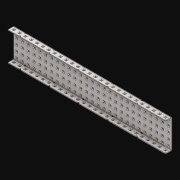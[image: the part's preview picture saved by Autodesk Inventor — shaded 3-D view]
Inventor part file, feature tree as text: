
AUTODESK INVENTOR PART (.ipt)
format: ipt  version: 2021 (Build 250183000, 183)  size: 3,673,600 bytes
history: native  units: in
note: dims shown in document units (in); Inventor stores cm internally (conversion verified against a paired STEP export)
features: extrude x190, other x189, sketch x4, thicken_offset x3, pattern_linear x3, imported_body x1
ambient origin geometry x8: Origin, YZ Plane, XZ Plane, XY Plane, X Axis, Y Axis, Z Axis, Center Point
bodies: Solid1 (feature_tree)
feature tree (390):
  thicken_offset  "Thicken1"
  thicken_offset  "Thicken2"
  thicken_offset  "Thicken3"
  pattern_linear  "Rectangular Pattern1"  Spacing1=0.001in  [1 undecoded]
  pattern_linear  "Rectangular Pattern2"  Spacing1=0.001in  [1 undecoded]
  pattern_linear  "Rectangular Pattern3"  Spacing1=0.182in  [1 undecoded]
  extrude  "Extrusion1"  Depth=0.063in TaperAngle=0.0deg
  sketch  "Sketch1"  dims[d0=0.001in]
  other  "Srf1"
  sketch  "Sketch2"  dims[d1=0.001in]
  other  "Srf2"
  sketch  "Sketch3"  dims[d2=0.001in]
  other  "Srf3"
  other  "Srf4"
  other  "Srf5"
  other  "Srf6"
  other  "Srf7"
  other  "Srf8"
  other  "Srf9"
  other  "Srf10"
  other  "Srf11"
  other  "Srf12"
  other  "Srf13"
  other  "Srf14"
  other  "Srf15"
  other  "Srf16"
  other  "Srf17"
  other  "Srf18"
  other  "Srf19"
  other  "Srf20"
  other  "Srf21"
  other  "Srf22"
  other  "Srf23"
  other  "Srf24"
  other  "Srf25"
  other  "Srf26"
  other  "Srf27"
  other  "Srf28"
  other  "Srf29"
  other  "Srf38"
  other  "Srf39"
  other  "Srf40"
  other  "Srf41"
  other  "Srf42"
  other  "Srf43"
  other  "Srf44"
  other  "Srf45"
  other  "Srf46"
  other  "Srf47"
  other  "Srf48"
  other  "Srf49"
  other  "Srf50"
  other  "Srf51"
  other  "Srf52"
  other  "Srf53"
  other  "Srf54"
  other  "Srf55"
  other  "Srf56"
  other  "Srf57"
  other  "Srf58"
  other  "Srf59"
  other  "Srf60"
  other  "Srf61"
  other  "Srf62"
  other  "Srf63"
  other  "Srf72"
  other  "Srf73"
  other  "Srf74"
  other  "Srf75"
  other  "Srf76"
  other  "Srf77"
  other  "Srf78"
  other  "Srf79"
  other  "Srf80"
  other  "Srf81"
  other  "Srf82"
  other  "Srf83"
  other  "Srf84"
  other  "Srf85"
  other  "Srf86"
  other  "Srf87"
  other  "Srf88"
  other  "Srf89"
  other  "Srf90"
  other  "Srf91"
  other  "Srf92"
  other  "Srf93"
  other  "Srf94"
  other  "Srf95"
  other  "Srf96"
  other  "Srf97"
  other  "Srf106"
  other  "Srf107"
  other  "Srf108"
  other  "Srf109"
  other  "Srf110"
  other  "Srf111"
  other  "Srf112"
  other  "Srf113"
  other  "Srf114"
  other  "Srf115"
  other  "Srf116"
  other  "Srf117"
  other  "Srf118"
  other  "Srf119"
  other  "Srf120"
  other  "Srf121"
  other  "Srf122"
  other  "Srf123"
  other  "Srf124"
  other  "Srf125"
  other  "Srf126"
  other  "Srf127"
  other  "Srf128"
  other  "Srf129"
  other  "Srf130"
  other  "Srf131"
  other  "Srf132"
  other  "Srf141"
  other  "Srf142"
  other  "Srf143"
  other  "Srf144"
  other  "Srf145"
  other  "Srf146"
  other  "Srf147"
  other  "Srf148"
  other  "Srf149"
  other  "Srf150"
  other  "Srf151"
  other  "Srf152"
  other  "Srf153"
  other  "Srf154"
  other  "Srf155"
  other  "Srf156"
  other  "Srf157"
  other  "Srf158"
  other  "Srf159"
  other  "Srf160"
  other  "Srf161"
  other  "Srf162"
  other  "Srf163"
  other  "Srf164"
  other  "Srf165"
  other  "Srf166"
  other  "Srf167"
  other  "Srf176"
  other  "Srf177"
  other  "Srf178"
  other  "Srf179"
  other  "Srf180"
  other  "Srf181"
  other  "Srf182"
  other  "Srf183"
  other  "Srf184"
  other  "Srf185"
  other  "Srf186"
  other  "Srf187"
  other  "Srf188"
  other  "Srf189"
  other  "Srf190"
  other  "Srf191"
  other  "Srf192"
  other  "Srf193"
  other  "Srf194"
  other  "Srf195"
  other  "Srf196"
  other  "Srf197"
  other  "Srf198"
  other  "Srf199"
  other  "Srf200"
  other  "Srf201"
  other  "Srf202"
  other  "Srf211"
  other  "Srf212"
  other  "Srf213"
  other  "Srf214"
  other  "Srf215"
  other  "Srf216"
  other  "Srf217"
  other  "Srf218"
  other  "Srf219"
  other  "Srf220"
  other  "Srf221"
  other  "Srf222"
  other  "Srf223"
  other  "Srf224"
  other  "Srf225"
  other  "Srf226"
  other  "Srf227"
  other  "Srf228"
  other  "Srf229"
  other  "Srf230"
  other  "Srf231"
  other  "Srf232"
  other  "Srf233"
  other  "Srf234"
  other  "Srf235"
  other  "Srf236"
  other  "Srf237"
  sketch  "Sketch4"  dims[d3=0.001in d4=0.001in d5=0.001in d6=0.182in d7=0.063in d8=0.0in d9=0.182in d10=0.063in d11=0.0in d12=0.182in d13=0.063in d14=0.0in d17=0.5in d18=10.6299in d20=0.5in d21=10.6299in d23=0.5in d24=1.9685in d26=0.5in d27=4.0in d28=0.0in]
  imported_body  "Imported1"
  extrude  "ExtrusionSrf1"  Depth=4.0in
  extrude  "ExtrusionSrf2"  Depth=0.063in TaperAngle=0.0deg
  extrude  "ExtrusionSrf3"  Depth=4.0in
  extrude  "ExtrusionSrf4"  Depth=0.063in TaperAngle=0.0deg
  extrude  "ExtrusionSrf5"  Depth=0.5in
  extrude  "ExtrusionSrf6"  Depth=4.0in
  extrude  "ExtrusionSrf7"  Depth=0.5in
  extrude  "ExtrusionSrf8"  Depth=4.0in
  extrude  "ExtrusionSrf9"  Depth=0.5in
  extrude  "ExtrusionSrf10"  Depth=0.5in
  extrude  "ExtrusionSrf11"  Depth=4.0in
  extrude  "ExtrusionSrf12"  TaperAngle=0.0deg  [1 undecoded]
  extrude  "ExtrusionSrf13"  [1 undecoded]
  extrude  "ExtrusionSrf14"  [1 undecoded]
  extrude  "ExtrusionSrf15"  [1 undecoded]
  extrude  "ExtrusionSrf16"  [1 undecoded]
  extrude  "ExtrusionSrf17"  [1 undecoded]
  extrude  "ExtrusionSrf18"  [1 undecoded]
  extrude  "ExtrusionSrf19"  [1 undecoded]
  extrude  "ExtrusionSrf20"  [1 undecoded]
  extrude  "ExtrusionSrf21"  [1 undecoded]
  extrude  "ExtrusionSrf22"  [1 undecoded]
  extrude  "ExtrusionSrf23"  [1 undecoded]
  extrude  "ExtrusionSrf24"  [1 undecoded]
  extrude  "ExtrusionSrf25"  [1 undecoded]
  extrude  "ExtrusionSrf26"  [1 undecoded]
  extrude  "ExtrusionSrf27"  [1 undecoded]
  extrude  "ExtrusionSrf28"  [1 undecoded]
  extrude  "ExtrusionSrf29"  [1 undecoded]
  extrude  "ExtrusionSrf38"  [1 undecoded]
  extrude  "ExtrusionSrf39"  [1 undecoded]
  extrude  "ExtrusionSrf40"  [1 undecoded]
  extrude  "ExtrusionSrf41"  [1 undecoded]
  extrude  "ExtrusionSrf42"  [1 undecoded]
  extrude  "ExtrusionSrf43"  [1 undecoded]
  extrude  "ExtrusionSrf44"  [1 undecoded]
  extrude  "ExtrusionSrf45"  [1 undecoded]
  extrude  "ExtrusionSrf46"  [1 undecoded]
  extrude  "ExtrusionSrf47"  [1 undecoded]
  extrude  "ExtrusionSrf48"  [1 undecoded]
  extrude  "ExtrusionSrf49"  [1 undecoded]
  extrude  "ExtrusionSrf50"  [1 undecoded]
  extrude  "ExtrusionSrf51"  [1 undecoded]
  extrude  "ExtrusionSrf52"  [1 undecoded]
  extrude  "ExtrusionSrf53"  [1 undecoded]
  extrude  "ExtrusionSrf54"  [1 undecoded]
  extrude  "ExtrusionSrf55"  [1 undecoded]
  extrude  "ExtrusionSrf56"  [1 undecoded]
  extrude  "ExtrusionSrf57"  [1 undecoded]
  extrude  "ExtrusionSrf58"  [1 undecoded]
  extrude  "ExtrusionSrf59"  [1 undecoded]
  extrude  "ExtrusionSrf60"  [1 undecoded]
  extrude  "ExtrusionSrf61"  [1 undecoded]
  extrude  "ExtrusionSrf62"  [1 undecoded]
  extrude  "ExtrusionSrf63"  [1 undecoded]
  extrude  "ExtrusionSrf72"  [1 undecoded]
  extrude  "ExtrusionSrf73"  [1 undecoded]
  extrude  "ExtrusionSrf74"  [1 undecoded]
  extrude  "ExtrusionSrf75"  [1 undecoded]
  extrude  "ExtrusionSrf76"  [1 undecoded]
  extrude  "ExtrusionSrf77"  [1 undecoded]
  extrude  "ExtrusionSrf78"  [1 undecoded]
  extrude  "ExtrusionSrf79"  [1 undecoded]
  extrude  "ExtrusionSrf80"  [1 undecoded]
  extrude  "ExtrusionSrf81"  [1 undecoded]
  extrude  "ExtrusionSrf82"  [1 undecoded]
  extrude  "ExtrusionSrf83"  [1 undecoded]
  extrude  "ExtrusionSrf84"  [1 undecoded]
  extrude  "ExtrusionSrf85"  [1 undecoded]
  extrude  "ExtrusionSrf86"  [1 undecoded]
  extrude  "ExtrusionSrf87"  [1 undecoded]
  extrude  "ExtrusionSrf88"  [1 undecoded]
  extrude  "ExtrusionSrf89"  [1 undecoded]
  extrude  "ExtrusionSrf90"  [1 undecoded]
  extrude  "ExtrusionSrf91"  [1 undecoded]
  extrude  "ExtrusionSrf92"  [1 undecoded]
  extrude  "ExtrusionSrf93"  [1 undecoded]
  extrude  "ExtrusionSrf94"  [1 undecoded]
  extrude  "ExtrusionSrf95"  [1 undecoded]
  extrude  "ExtrusionSrf96"  [1 undecoded]
  extrude  "ExtrusionSrf97"  [1 undecoded]
  extrude  "ExtrusionSrf106"  [1 undecoded]
  extrude  "ExtrusionSrf107"  [1 undecoded]
  extrude  "ExtrusionSrf108"  [1 undecoded]
  extrude  "ExtrusionSrf109"  [1 undecoded]
  extrude  "ExtrusionSrf110"  [1 undecoded]
  extrude  "ExtrusionSrf111"  [1 undecoded]
  extrude  "ExtrusionSrf112"  [1 undecoded]
  extrude  "ExtrusionSrf113"  [1 undecoded]
  extrude  "ExtrusionSrf114"  [1 undecoded]
  extrude  "ExtrusionSrf115"  [1 undecoded]
  extrude  "ExtrusionSrf116"  [1 undecoded]
  extrude  "ExtrusionSrf117"  [1 undecoded]
  extrude  "ExtrusionSrf118"  [1 undecoded]
  extrude  "ExtrusionSrf119"  [1 undecoded]
  extrude  "ExtrusionSrf120"  [1 undecoded]
  extrude  "ExtrusionSrf121"  [1 undecoded]
  extrude  "ExtrusionSrf122"  [1 undecoded]
  extrude  "ExtrusionSrf123"  [1 undecoded]
  extrude  "ExtrusionSrf124"  [1 undecoded]
  extrude  "ExtrusionSrf125"  [1 undecoded]
  extrude  "ExtrusionSrf126"  [1 undecoded]
  extrude  "ExtrusionSrf127"  [1 undecoded]
  extrude  "ExtrusionSrf128"  [1 undecoded]
  extrude  "ExtrusionSrf129"  [1 undecoded]
  extrude  "ExtrusionSrf130"  [1 undecoded]
  extrude  "ExtrusionSrf131"  [1 undecoded]
  extrude  "ExtrusionSrf132"  [1 undecoded]
  extrude  "ExtrusionSrf141"  [1 undecoded]
  extrude  "ExtrusionSrf142"  [1 undecoded]
  extrude  "ExtrusionSrf143"  [1 undecoded]
  extrude  "ExtrusionSrf144"  [1 undecoded]
  extrude  "ExtrusionSrf145"  [1 undecoded]
  extrude  "ExtrusionSrf146"  [1 undecoded]
  extrude  "ExtrusionSrf147"  [1 undecoded]
  extrude  "ExtrusionSrf148"  [1 undecoded]
  extrude  "ExtrusionSrf149"  [1 undecoded]
  extrude  "ExtrusionSrf150"  [1 undecoded]
  extrude  "ExtrusionSrf151"  [1 undecoded]
  extrude  "ExtrusionSrf152"  [1 undecoded]
  extrude  "ExtrusionSrf153"  [1 undecoded]
  extrude  "ExtrusionSrf154"  [1 undecoded]
  extrude  "ExtrusionSrf155"  [1 undecoded]
  extrude  "ExtrusionSrf156"  [1 undecoded]
  extrude  "ExtrusionSrf157"  [1 undecoded]
  extrude  "ExtrusionSrf158"  [1 undecoded]
  extrude  "ExtrusionSrf159"  [1 undecoded]
  extrude  "ExtrusionSrf160"  [1 undecoded]
  extrude  "ExtrusionSrf161"  [1 undecoded]
  extrude  "ExtrusionSrf162"  [1 undecoded]
  extrude  "ExtrusionSrf163"  [1 undecoded]
  extrude  "ExtrusionSrf164"  [1 undecoded]
  extrude  "ExtrusionSrf165"  [1 undecoded]
  extrude  "ExtrusionSrf166"  [1 undecoded]
  extrude  "ExtrusionSrf167"  [1 undecoded]
  extrude  "ExtrusionSrf176"  [1 undecoded]
  extrude  "ExtrusionSrf177"  [1 undecoded]
  extrude  "ExtrusionSrf178"  [1 undecoded]
  extrude  "ExtrusionSrf179"  [1 undecoded]
  extrude  "ExtrusionSrf180"  [1 undecoded]
  extrude  "ExtrusionSrf181"  [1 undecoded]
  extrude  "ExtrusionSrf182"  [1 undecoded]
  extrude  "ExtrusionSrf183"  [1 undecoded]
  extrude  "ExtrusionSrf184"  [1 undecoded]
  extrude  "ExtrusionSrf185"  [1 undecoded]
  extrude  "ExtrusionSrf186"  [1 undecoded]
  extrude  "ExtrusionSrf187"  [1 undecoded]
  extrude  "ExtrusionSrf188"  [1 undecoded]
  extrude  "ExtrusionSrf189"  [1 undecoded]
  extrude  "ExtrusionSrf190"  [1 undecoded]
  extrude  "ExtrusionSrf191"  [1 undecoded]
  extrude  "ExtrusionSrf192"  [1 undecoded]
  extrude  "ExtrusionSrf193"  [1 undecoded]
  extrude  "ExtrusionSrf194"  [1 undecoded]
  extrude  "ExtrusionSrf195"  [1 undecoded]
  extrude  "ExtrusionSrf196"  [1 undecoded]
  extrude  "ExtrusionSrf197"  [1 undecoded]
  extrude  "ExtrusionSrf198"  [1 undecoded]
  extrude  "ExtrusionSrf199"  [1 undecoded]
  extrude  "ExtrusionSrf200"  [1 undecoded]
  extrude  "ExtrusionSrf201"  [1 undecoded]
  extrude  "ExtrusionSrf202"  [1 undecoded]
  extrude  "ExtrusionSrf211"  [1 undecoded]
  extrude  "ExtrusionSrf212"  [1 undecoded]
  extrude  "ExtrusionSrf213"  [1 undecoded]
  extrude  "ExtrusionSrf214"  [1 undecoded]
  extrude  "ExtrusionSrf215"  [1 undecoded]
  extrude  "ExtrusionSrf216"  [1 undecoded]
  extrude  "ExtrusionSrf217"  [1 undecoded]
  extrude  "ExtrusionSrf218"  [1 undecoded]
  extrude  "ExtrusionSrf219"  [1 undecoded]
  extrude  "ExtrusionSrf220"  [1 undecoded]
  extrude  "ExtrusionSrf221"  [1 undecoded]
  extrude  "ExtrusionSrf222"  [1 undecoded]
  extrude  "ExtrusionSrf223"  [1 undecoded]
  extrude  "ExtrusionSrf224"  [1 undecoded]
  extrude  "ExtrusionSrf225"  [1 undecoded]
  extrude  "ExtrusionSrf226"  [1 undecoded]
  extrude  "ExtrusionSrf227"  [1 undecoded]
  extrude  "ExtrusionSrf228"  [1 undecoded]
  extrude  "ExtrusionSrf229"  [1 undecoded]
  extrude  "ExtrusionSrf230"  [1 undecoded]
  extrude  "ExtrusionSrf231"  [1 undecoded]
  extrude  "ExtrusionSrf232"  [1 undecoded]
  extrude  "ExtrusionSrf233"  [1 undecoded]
  extrude  "ExtrusionSrf234"  [1 undecoded]
  extrude  "ExtrusionSrf235"  [1 undecoded]
  extrude  "ExtrusionSrf236"  [1 undecoded]
  extrude  "ExtrusionSrf237"  [1 undecoded]
note: 181 required parameter values undecoded (feature->parameter linkage not recoverable at this tier; creation-order binding heuristic only, values carry confidence <= 0.55)
